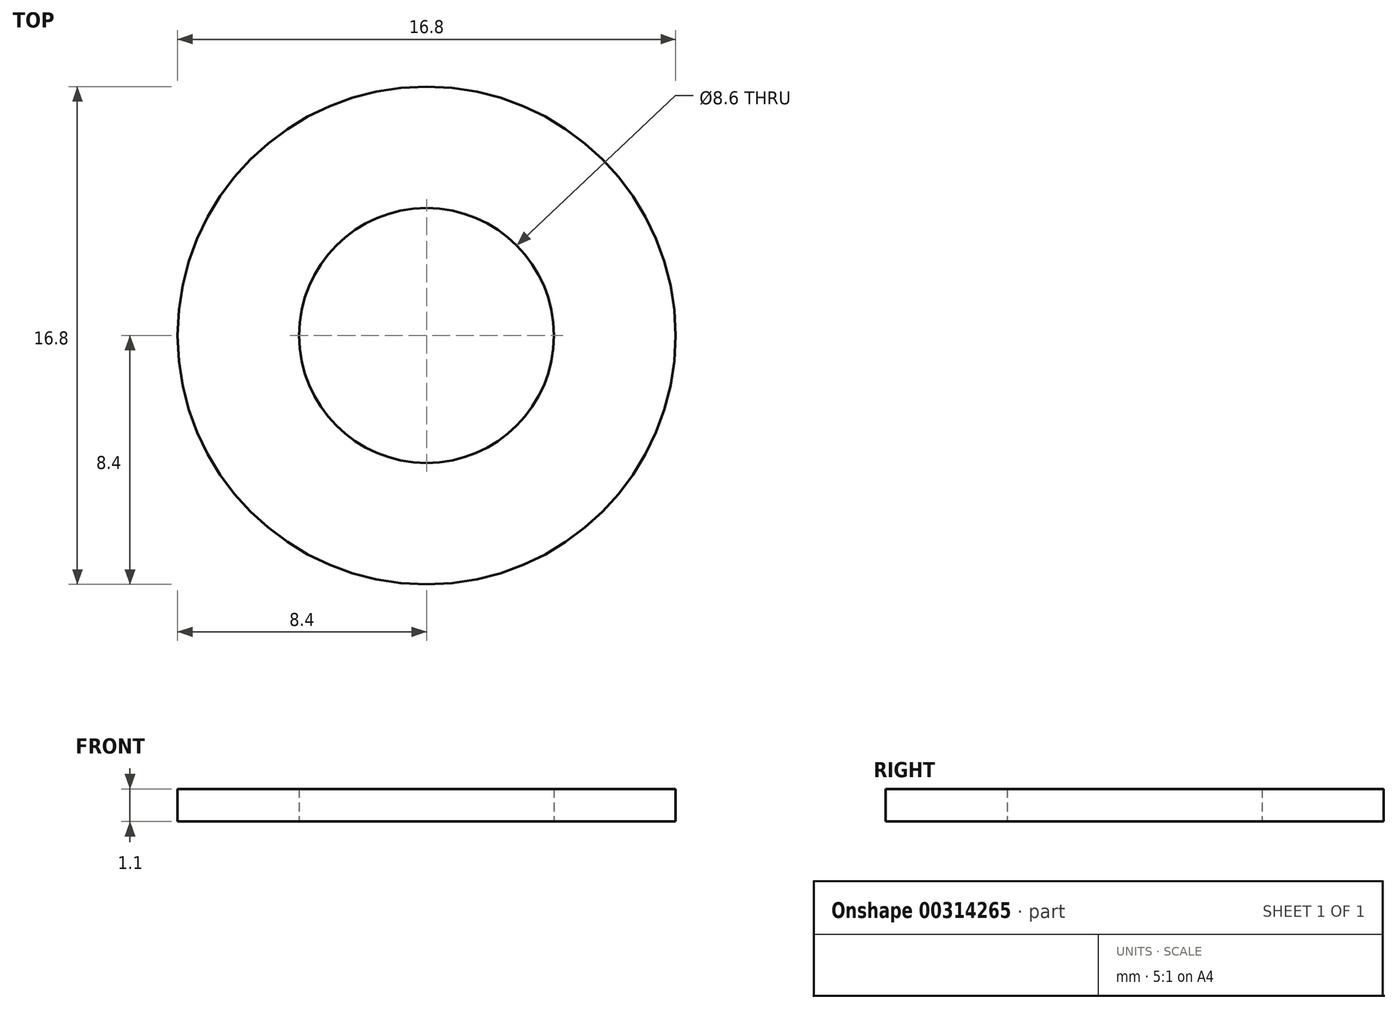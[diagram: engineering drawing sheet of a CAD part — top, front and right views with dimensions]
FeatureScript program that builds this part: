
annotation { "Feature Type Name" : "Feature", "Feature Type Description" : "" }
export const myFeature = defineFeature(function(context is Context, id is Id, definition is map)
    precondition{}
    {
        {
            var Q0;
            Q0=qCreatedBy(makeId("Top.planeOp"),FACE);
            var sketch = newSketch(context, id + "F0", { "sketchPlane" : qUnion([Q0])});
            skCircle(sketch, "E0", {"center": v(0, 0) * mm, "radius": 4.3 * mm});
            skCircle(sketch, "E1", {"center": v(0, 0) * mm, "radius": 8.4 * mm});
            skSolve(sketch);
        }
        {
            var Q0;
            Q0 = qSketchRegion(id + "F0", true);
            extrude(context, id + "F1", {"entities" : qUnion([Q0]), "depth" : 1.1 * mm});
        }
    });
